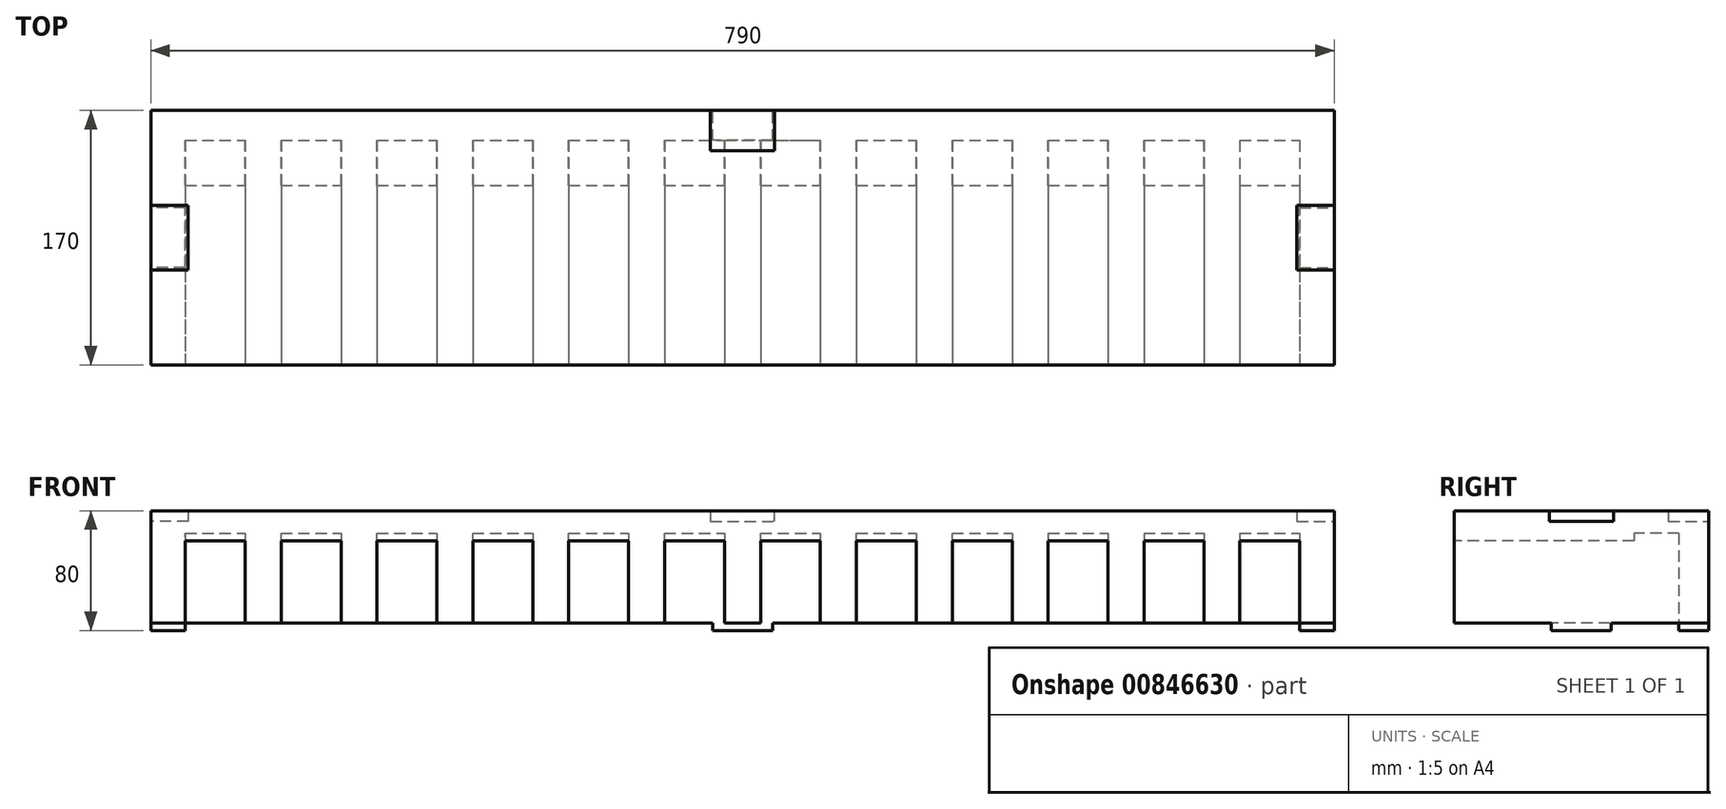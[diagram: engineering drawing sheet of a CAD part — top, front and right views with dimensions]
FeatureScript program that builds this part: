
annotation { "Feature Type Name" : "Feature", "Feature Type Description" : "" }
export const myFeature = defineFeature(function(context is Context, id is Id, definition is map)
    precondition{}
    {
        {
            var Q0;
            Q0=qCreatedBy(makeId("Front.planeOp"),FACE);
            var sketch = newSketch(context, id + "F0", { "sketchPlane" : qUnion([Q0])});
            skLineSegment(sketch, "E0.bottom", {"start": v(-404.78, 0) * mm, "end": v(385.22, 0) * mm});
            skLineSegment(sketch, "E0.top", {"start": v(-404.78, -75) * mm, "end": v(385.22, -75) * mm});
            skLineSegment(sketch, "E0.left", {"start": v(-404.78, 0) * mm, "end": v(-404.78, -75) * mm});
            skLineSegment(sketch, "E0.right", {"start": v(385.22, 0) * mm, "end": v(385.22, -75) * mm});
            skSolve(sketch);
        }
        {
            var Q0;
            Q0=makeQuery(id+"F0.imprint","IMPRINT",FACE,{"disambiguationData":[TD([[makeQuery(id+"F0.imprint","IMPRINT",EDGE,{"derivedFrom":sQuery(id+"F0.wireOp",EDGE,"E0.bottom")}),-1.0]])]});
            extrude(context, id + "F1", {"entities" : qUnion([Q0]), "offsetDistance" : 25 * mm, "depth" : 170 * mm});
        }
        {
            var Q0;
            Q0=makeQuery(id+"F1.opExtrude","CAP_FACE",FACE,{"disambiguationData":[OSD([sQuery(id+"F0.wireOp",EDGE,"E0.bottom"),sQuery(id+"F0.wireOp",EDGE,"E0.top"),sQuery(id+"F0.wireOp",EDGE,"E0.left"),sQuery(id+"F0.wireOp",EDGE,"E0.right")])],"isStart":false});
            var sketch = newSketch(context, id + "F2", { "sketchPlane" : qUnion([Q0])});
            skLineSegment(sketch, "E1.bottom", {"start": v(-381.78, -75) * mm, "end": v(-341.78, -75) * mm});
            skLineSegment(sketch, "E1.top", {"start": v(-381.78, -20) * mm, "end": v(-341.78, -20) * mm});
            skLineSegment(sketch, "E1.left", {"start": v(-381.78, -75) * mm, "end": v(-381.78, -20) * mm});
            skLineSegment(sketch, "E1.right", {"start": v(-341.78, -75) * mm, "end": v(-341.78, -20) * mm});
            skLineSegment(sketch, "E2.bottom", {"start": v(-317.78, -75) * mm, "end": v(-277.78, -75) * mm});
            skLineSegment(sketch, "E2.top", {"start": v(-317.78, -20) * mm, "end": v(-277.78, -20) * mm});
            skLineSegment(sketch, "E2.left", {"start": v(-317.78, -75) * mm, "end": v(-317.78, -20) * mm});
            skLineSegment(sketch, "E2.right", {"start": v(-277.78, -75) * mm, "end": v(-277.78, -20) * mm});
            skLineSegment(sketch, "E3.bottom", {"start": v(-253.78, -75) * mm, "end": v(-213.78, -75) * mm});
            skLineSegment(sketch, "E3.top", {"start": v(-253.78, -20) * mm, "end": v(-213.78, -20) * mm});
            skLineSegment(sketch, "E3.left", {"start": v(-253.78, -75) * mm, "end": v(-253.78, -20) * mm});
            skLineSegment(sketch, "E3.right", {"start": v(-213.78, -75) * mm, "end": v(-213.78, -20) * mm});
            skPoint(sketch, "E4.oppositeSnap0", {"position": v(-233.78, -20) * mm});
            skLineSegment(sketch, "E4.bottom", {"start": v(-189.78, -75) * mm, "end": v(-149.78, -75) * mm});
            skLineSegment(sketch, "E4.top", {"start": v(-189.78, -20) * mm, "end": v(-149.78, -20) * mm});
            skLineSegment(sketch, "E4.left", {"start": v(-189.78, -75) * mm, "end": v(-189.78, -20) * mm});
            skLineSegment(sketch, "E4.right", {"start": v(-149.78, -75) * mm, "end": v(-149.78, -20) * mm});
            skLineSegment(sketch, "E5.bottom", {"start": v(-125.78, -75) * mm, "end": v(-85.78, -75) * mm});
            skLineSegment(sketch, "E5.top", {"start": v(-125.78, -20) * mm, "end": v(-85.78, -20) * mm});
            skLineSegment(sketch, "E5.left", {"start": v(-125.78, -75) * mm, "end": v(-125.78, -20) * mm});
            skLineSegment(sketch, "E5.right", {"start": v(-85.78, -75) * mm, "end": v(-85.78, -20) * mm});
            skLineSegment(sketch, "E6.bottom", {"start": v(-61.78, -75) * mm, "end": v(-21.78, -75) * mm});
            skLineSegment(sketch, "E6.top", {"start": v(-61.78, -20) * mm, "end": v(-21.78, -20) * mm});
            skLineSegment(sketch, "E6.left", {"start": v(-61.78, -75) * mm, "end": v(-61.78, -20) * mm});
            skLineSegment(sketch, "E6.right", {"start": v(-21.78, -75) * mm, "end": v(-21.78, -20) * mm});
            skLineSegment(sketch, "E7.bottom", {"start": v(2.22, -75) * mm, "end": v(42.22, -75) * mm});
            skLineSegment(sketch, "E7.top", {"start": v(2.22, -20) * mm, "end": v(42.22, -20) * mm});
            skLineSegment(sketch, "E7.left", {"start": v(2.22, -75) * mm, "end": v(2.22, -20) * mm});
            skLineSegment(sketch, "E7.right", {"start": v(42.22, -75) * mm, "end": v(42.22, -20) * mm});
            skLineSegment(sketch, "E8.bottom", {"start": v(66.22, -75) * mm, "end": v(106.22, -75) * mm});
            skLineSegment(sketch, "E8.top", {"start": v(66.22, -20) * mm, "end": v(106.22, -20) * mm});
            skLineSegment(sketch, "E8.left", {"start": v(66.22, -75) * mm, "end": v(66.22, -20) * mm});
            skLineSegment(sketch, "E8.right", {"start": v(106.22, -75) * mm, "end": v(106.22, -20) * mm});
            skLineSegment(sketch, "E9.bottom", {"start": v(130.22, -75) * mm, "end": v(170.22, -75) * mm});
            skLineSegment(sketch, "E9.top", {"start": v(130.22, -20) * mm, "end": v(170.22, -20) * mm});
            skLineSegment(sketch, "E9.left", {"start": v(130.22, -75) * mm, "end": v(130.22, -20) * mm});
            skLineSegment(sketch, "E9.right", {"start": v(170.22, -75) * mm, "end": v(170.22, -20) * mm});
            skLineSegment(sketch, "E10.bottom", {"start": v(194.22, -20) * mm, "end": v(234.22, -20) * mm});
            skLineSegment(sketch, "E10.top", {"start": v(194.22, -75) * mm, "end": v(234.22, -75) * mm});
            skLineSegment(sketch, "E10.left", {"start": v(194.22, -20) * mm, "end": v(194.22, -75) * mm});
            skLineSegment(sketch, "E10.right", {"start": v(234.22, -20) * mm, "end": v(234.22, -75) * mm});
            skLineSegment(sketch, "E11.bottom", {"start": v(258.22, -20) * mm, "end": v(298.22, -20) * mm});
            skLineSegment(sketch, "E11.top", {"start": v(258.22, -75) * mm, "end": v(298.22, -75) * mm});
            skLineSegment(sketch, "E11.left", {"start": v(258.22, -20) * mm, "end": v(258.22, -75) * mm});
            skLineSegment(sketch, "E11.right", {"start": v(298.22, -20) * mm, "end": v(298.22, -75) * mm});
            skLineSegment(sketch, "E12.bottom", {"start": v(322.22, -20) * mm, "end": v(362.22, -20) * mm});
            skLineSegment(sketch, "E12.top", {"start": v(322.22, -75) * mm, "end": v(362.22, -75) * mm});
            skLineSegment(sketch, "E12.left", {"start": v(322.22, -20) * mm, "end": v(322.22, -75) * mm});
            skLineSegment(sketch, "E12.right", {"start": v(362.22, -20) * mm, "end": v(362.22, -75) * mm});
            skSolve(sketch);
        }
        {
            var Q0;
            Q0=qSketchRegion(id+"F2",true);
            extrude(context, id + "F3", {"entities" : qUnion([Q0]), "operationType" : NewBodyOperationType.REMOVE, "oppositeDirection" : true, "offsetDistance" : 25 * mm, "depth" : 150 * mm});
        }
        {
            var Q0;
            Q0=makeQuery(id+"F1.opExtrude","SWEPT_FACE",FACE,{"disambiguationData":[OSD([sQuery(id+"F0.wireOp",EDGE,"E0.left")])]});
            var sketch = newSketch(context, id + "F4", { "sketchPlane" : qUnion([Q0])});
            skLineSegment(sketch, "E13", {"start": v(85, 0) * mm, "end": v(106.5, 0) * mm});
            skLineSegment(sketch, "E14", {"start": v(106.5, 0) * mm, "end": v(106.5, -7) * mm});
            skLineSegment(sketch, "E15", {"start": v(106.5, -7) * mm, "end": v(63.5, -7) * mm});
            skLineSegment(sketch, "E16", {"start": v(63.5, -7) * mm, "end": v(63.5, 0) * mm});
            skLineSegment(sketch, "E17", {"start": v(63.5, 0) * mm, "end": v(85, 0) * mm});
            skLineSegment(sketch, "E18", {"start": v(105, -75) * mm, "end": v(105, -80) * mm});
            skLineSegment(sketch, "E19", {"start": v(105, -80) * mm, "end": v(65, -80) * mm});
            skLineSegment(sketch, "E20", {"start": v(65, -80) * mm, "end": v(65, -75) * mm});
            skLineSegment(sketch, "E21", {"start": v(65, -75) * mm, "end": v(105, -75) * mm});
            skSolve(sketch);
        }
        {
            var Q0;
            Q0=makeQuery(id+"F4.imprint","IMPRINT",FACE,{"disambiguationData":[TD([[makeQuery(id+"F4.imprint","IMPRINT",EDGE,{"derivedFrom":sQuery(id+"F4.wireOp",EDGE,"E13")}),1.0]])]});
            var Q1;
            Q1=sQuery(id+"F4.wireOp",EDGE,"E16");
            var Q2;
            Q2=sQuery(id+"F4.wireOp",EDGE,"E15");
            var Q3;
            Q3=sQuery(id+"F4.wireOp",EDGE,"E17");
            var Q4;
            Q4=sQuery(id+"F4.wireOp",EDGE,"E13");
            var Q5;
            Q5=sQuery(id+"F4.wireOp",EDGE,"E14");
            extrude(context, id + "F5", {"entities" : qUnion([Q0]), "operationType" : NewBodyOperationType.REMOVE, "surfaceEntities" : qUnion([Q1, Q2, Q3, Q4, Q5]), "oppositeDirection" : true, "depth" : 25 * mm, "offsetDistance" : 25 * mm});
        }
        {
            var Q0;
            Q0=makeQuery(id+"F4.imprint","IMPRINT",FACE,{"disambiguationData":[TD([[makeQuery(id+"F4.imprint","IMPRINT",EDGE,{"derivedFrom":sQuery(id+"F4.wireOp",EDGE,"E18")}),-1.0]])]});
            var Q1;
            Q1=sQuery(id+"F4.wireOp",EDGE,"xgbccaoA-wlaa-1WH6-teic-Xw8wp0V9t22Q");
            var Q2;
            Q2=sQuery(id+"F4.wireOp",EDGE,"E20");
            var Q3;
            Q3=sQuery(id+"F4.wireOp",EDGE,"E19");
            var Q4;
            Q4=sQuery(id+"F4.wireOp",EDGE,"RcdgaTME-gTL4-fPj2-lDTn-aMnh3h9srcoK");
            var Q5;
            Q5=sQuery(id+"F4.wireOp",EDGE,"E18");
            extrude(context, id + "F6", {"entities" : qUnion([Q0]), "operationType" : NewBodyOperationType.ADD, "surfaceEntities" : qUnion([Q1, Q2, Q3, Q4, Q5]), "oppositeDirection" : true, "depth" : 23 * mm, "offsetDistance" : 25 * mm});
        }
        {
            var Q0;
            Q0=makeQuery(id+"F1.opExtrude","SWEPT_FACE",FACE,{"disambiguationData":[OSD([sQuery(id+"F0.wireOp",EDGE,"E0.right")])]});
            var sketch = newSketch(context, id + "F7", { "sketchPlane" : qUnion([Q0])});
            skLineSegment(sketch, "E22.bottom", {"start": v(-105, -75) * mm, "end": v(-65, -75) * mm});
            skLineSegment(sketch, "E22.top", {"start": v(-105, -80) * mm, "end": v(-65, -80) * mm});
            skLineSegment(sketch, "E22.left", {"start": v(-105, -75) * mm, "end": v(-105, -80) * mm});
            skLineSegment(sketch, "E22.right", {"start": v(-65, -75) * mm, "end": v(-65, -80) * mm});
            skSolve(sketch);
        }
        {
            var Q0;
            Q0 = qSketchRegion(id + "F7", true);
            extrude(context, id + "F8", {"entities" : qUnion([Q0]), "operationType" : NewBodyOperationType.ADD, "oppositeDirection" : true, "depth" : 23 * mm, "offsetDistance" : 25 * mm});
        }
        {
            var Q0;
            Q0=makeQuery(id+"F8.boolean.opBoolean","MERGE",FACE,{"derivedFrom":[makeQuery(id+"F1.opExtrude","SWEPT_FACE",FACE,{"disambiguationData":[OSD([sQuery(id+"F0.wireOp",EDGE,"E0.right")])]}),makeQuery(id+"F8.opExtrude","CAP_FACE",FACE,{"disambiguationData":[OSD([sQuery(id+"F7.wireOp",EDGE,"UznCfJuv-EcPL-bBKx-4p6R-uVAr0uQAR3AA.bottom"),sQuery(id+"F7.wireOp",EDGE,"UznCfJuv-EcPL-bBKx-4p6R-uVAr0uQAR3AA.top"),sQuery(id+"F7.wireOp",EDGE,"UznCfJuv-EcPL-bBKx-4p6R-uVAr0uQAR3AA.left"),sQuery(id+"F7.wireOp",EDGE,"UznCfJuv-EcPL-bBKx-4p6R-uVAr0uQAR3AA.right")])],"isStart":true})]});
            var sketch = newSketch(context, id + "F9", { "sketchPlane" : qUnion([Q0])});
            skLineSegment(sketch, "E23", {"start": v(-85, 0) * mm, "end": v(-63.5, 0) * mm});
            skLineSegment(sketch, "E24", {"start": v(-63.5, 0) * mm, "end": v(-63.5, -7) * mm});
            skLineSegment(sketch, "E25", {"start": v(-63.5, -7) * mm, "end": v(-106.5, -7) * mm});
            skLineSegment(sketch, "E26", {"start": v(-106.5, -7) * mm, "end": v(-106.5, 0) * mm});
            skLineSegment(sketch, "E27", {"start": v(-106.5, 0) * mm, "end": v(-85, 0) * mm});
            skSolve(sketch);
        }
        {
            var Q0;
            Q0 = qSketchRegion(id + "F9", true);
            extrude(context, id + "F10", {"entities" : qUnion([Q0]), "operationType" : NewBodyOperationType.REMOVE, "oppositeDirection" : true, "depth" : 25 * mm, "offsetDistance" : 25 * mm});
        }
        {
            var Q0;
            Q0=makeQuery(id+"F1.opExtrude","CAP_FACE",FACE,{"disambiguationData":[OSD([sQuery(id+"F0.wireOp",EDGE,"E0.bottom"),sQuery(id+"F0.wireOp",EDGE,"E0.top"),sQuery(id+"F0.wireOp",EDGE,"E0.left"),sQuery(id+"F0.wireOp",EDGE,"E0.right")])],"isStart":true});
            var sketch = newSketch(context, id + "F11", { "sketchPlane" : qUnion([Q0])});
            skLineSegment(sketch, "E28", {"start": v(9.78, 0) * mm, "end": v(31.28, 0) * mm});
            skLineSegment(sketch, "E29", {"start": v(31.28, 0) * mm, "end": v(31.28, -7) * mm});
            skLineSegment(sketch, "E30", {"start": v(31.28, -7) * mm, "end": v(-11.72, -7) * mm});
            skLineSegment(sketch, "E31", {"start": v(-11.72, -7) * mm, "end": v(-11.72, 0) * mm});
            skLineSegment(sketch, "E32", {"start": v(-11.72, 0) * mm, "end": v(9.78, 0) * mm});
            skSolve(sketch);
        }
        {
            var Q0;
            Q0 = qSketchRegion(id + "F11", true);
            extrude(context, id + "F12", {"entities" : qUnion([Q0]), "operationType" : NewBodyOperationType.REMOVE, "oppositeDirection" : true, "depth" : 27 * mm, "offsetDistance" : 25 * mm});
        }
        {
            var Q0;
            Q0=makeQuery(id+"F1.opExtrude","CAP_FACE",FACE,{"disambiguationData":[OSD([sQuery(id+"F0.wireOp",EDGE,"E0.bottom"),sQuery(id+"F0.wireOp",EDGE,"E0.top"),sQuery(id+"F0.wireOp",EDGE,"E0.left"),sQuery(id+"F0.wireOp",EDGE,"E0.right")])],"isStart":true});
            var sketch = newSketch(context, id + "F13", { "sketchPlane" : qUnion([Q0])});
            skLineSegment(sketch, "E33.bottom", {"start": v(29.78, -75) * mm, "end": v(-10.22, -75) * mm});
            skLineSegment(sketch, "E33.left", {"start": v(29.78, -75) * mm, "end": v(29.78, -69) * mm});
            skLineSegment(sketch, "E34", {"start": v(-10.22, -75) * mm, "end": v(-10.22, -80) * mm});
            skLineSegment(sketch, "E35", {"start": v(-10.22, -80) * mm, "end": v(29.78, -80) * mm});
            skLineSegment(sketch, "E36", {"start": v(29.78, -80) * mm, "end": v(29.78, -75) * mm});
            skSolve(sketch);
        }
        {
            var Q0;
            Q0 = qSketchRegion(id + "F13", true);
            extrude(context, id + "F14", {"entities" : qUnion([Q0]), "operationType" : NewBodyOperationType.ADD, "oppositeDirection" : true, "depth" : 20 * mm, "offsetDistance" : 25 * mm});
        }
        {
            var Q0;
            Q0=makeQuery(id+"F3.boolean.opBoolean","COPY",FACE,{"derivedFrom":makeQuery(id+"F3.opExtrude","SWEPT_FACE",FACE,{"disambiguationData":[OSD([sQuery(id+"F2.wireOp",EDGE,"E12.bottom")])]})});
            var sketch = newSketch(context, id + "F15", { "sketchPlane" : qUnion([Q0])});
            skLineSegment(sketch, "E37.bottom", {"start": v(-381.78, 50) * mm, "end": v(-341.78, 50) * mm});
            skLineSegment(sketch, "E37.top", {"start": v(-381.78, 20) * mm, "end": v(-341.78, 20) * mm});
            skLineSegment(sketch, "E37.left", {"start": v(-381.78, 50) * mm, "end": v(-381.78, 20) * mm});
            skLineSegment(sketch, "E37.right", {"start": v(-341.78, 50) * mm, "end": v(-341.78, 20) * mm});
            skLineSegment(sketch, "E38.bottom", {"start": v(-317.78, 50) * mm, "end": v(-277.78, 50) * mm});
            skLineSegment(sketch, "E38.top", {"start": v(-317.78, 20) * mm, "end": v(-277.78, 20) * mm});
            skLineSegment(sketch, "E38.left", {"start": v(-317.78, 50) * mm, "end": v(-317.78, 20) * mm});
            skLineSegment(sketch, "E38.right", {"start": v(-277.78, 50) * mm, "end": v(-277.78, 20) * mm});
            skLineSegment(sketch, "E39.bottom", {"start": v(-253.78, 50) * mm, "end": v(-213.78, 50) * mm});
            skLineSegment(sketch, "E39.top", {"start": v(-253.78, 20) * mm, "end": v(-213.78, 20) * mm});
            skLineSegment(sketch, "E39.left", {"start": v(-253.78, 50) * mm, "end": v(-253.78, 20) * mm});
            skLineSegment(sketch, "E39.right", {"start": v(-213.78, 50) * mm, "end": v(-213.78, 20) * mm});
            skLineSegment(sketch, "E40.bottom", {"start": v(-189.78, 50) * mm, "end": v(-149.78, 50) * mm});
            skLineSegment(sketch, "E40.top", {"start": v(-189.78, 20) * mm, "end": v(-149.78, 20) * mm});
            skLineSegment(sketch, "E40.left", {"start": v(-189.78, 50) * mm, "end": v(-189.78, 20) * mm});
            skLineSegment(sketch, "E40.right", {"start": v(-149.78, 50) * mm, "end": v(-149.78, 20) * mm});
            skLineSegment(sketch, "E41.bottom", {"start": v(-125.78, 50) * mm, "end": v(-85.78, 50) * mm});
            skLineSegment(sketch, "E41.top", {"start": v(-125.78, 20) * mm, "end": v(-85.78, 20) * mm});
            skLineSegment(sketch, "E41.left", {"start": v(-125.78, 50) * mm, "end": v(-125.78, 20) * mm});
            skLineSegment(sketch, "E41.right", {"start": v(-85.78, 50) * mm, "end": v(-85.78, 20) * mm});
            skLineSegment(sketch, "E42.bottom", {"start": v(-61.78, 50) * mm, "end": v(-21.78, 50) * mm});
            skLineSegment(sketch, "E42.top", {"start": v(-61.78, 20) * mm, "end": v(-21.78, 20) * mm});
            skLineSegment(sketch, "E42.left", {"start": v(-61.78, 50) * mm, "end": v(-61.78, 20) * mm});
            skLineSegment(sketch, "E42.right", {"start": v(-21.78, 50) * mm, "end": v(-21.78, 20) * mm});
            skLineSegment(sketch, "E43.bottom", {"start": v(2.22, 50) * mm, "end": v(42.22, 50) * mm});
            skLineSegment(sketch, "E43.top", {"start": v(2.22, 20) * mm, "end": v(42.22, 20) * mm});
            skLineSegment(sketch, "E43.left", {"start": v(2.22, 50) * mm, "end": v(2.22, 20) * mm});
            skLineSegment(sketch, "E43.right", {"start": v(42.22, 50) * mm, "end": v(42.22, 20) * mm});
            skLineSegment(sketch, "E44.bottom", {"start": v(66.22, 50) * mm, "end": v(106.22, 50) * mm});
            skLineSegment(sketch, "E44.top", {"start": v(66.22, 20) * mm, "end": v(106.22, 20) * mm});
            skLineSegment(sketch, "E44.left", {"start": v(66.22, 50) * mm, "end": v(66.22, 20) * mm});
            skLineSegment(sketch, "E44.right", {"start": v(106.22, 50) * mm, "end": v(106.22, 20) * mm});
            skPoint(sketch, "E45.firstSnap0", {"position": v(86.22, 50) * mm});
            skLineSegment(sketch, "E45.bottom", {"start": v(130.22, 50) * mm, "end": v(170.22, 50) * mm});
            skLineSegment(sketch, "E45.top", {"start": v(130.22, 20) * mm, "end": v(170.22, 20) * mm});
            skLineSegment(sketch, "E45.left", {"start": v(130.22, 50) * mm, "end": v(130.22, 20) * mm});
            skLineSegment(sketch, "E45.right", {"start": v(170.22, 50) * mm, "end": v(170.22, 20) * mm});
            skLineSegment(sketch, "E46.bottom", {"start": v(194.22, 50) * mm, "end": v(234.22, 50) * mm});
            skLineSegment(sketch, "E46.top", {"start": v(194.22, 20) * mm, "end": v(234.22, 20) * mm});
            skLineSegment(sketch, "E46.left", {"start": v(194.22, 50) * mm, "end": v(194.22, 20) * mm});
            skLineSegment(sketch, "E46.right", {"start": v(234.22, 50) * mm, "end": v(234.22, 20) * mm});
            skLineSegment(sketch, "E47.bottom", {"start": v(258.22, 50) * mm, "end": v(298.22, 50) * mm});
            skLineSegment(sketch, "E47.top", {"start": v(258.22, 20) * mm, "end": v(298.22, 20) * mm});
            skLineSegment(sketch, "E47.left", {"start": v(258.22, 50) * mm, "end": v(258.22, 20) * mm});
            skLineSegment(sketch, "E47.right", {"start": v(298.22, 50) * mm, "end": v(298.22, 20) * mm});
            skLineSegment(sketch, "E48.bottom", {"start": v(322.22, 50) * mm, "end": v(362.22, 50) * mm});
            skLineSegment(sketch, "E48.top", {"start": v(322.22, 20) * mm, "end": v(362.22, 20) * mm});
            skLineSegment(sketch, "E48.left", {"start": v(322.22, 50) * mm, "end": v(322.22, 20) * mm});
            skLineSegment(sketch, "E48.right", {"start": v(362.22, 50) * mm, "end": v(362.22, 20) * mm});
            skSolve(sketch);
        }
        {
            var Q0;
            Q0 = qSketchRegion(id + "F15", true);
            extrude(context, id + "F16", {"entities" : qUnion([Q0]), "operationType" : NewBodyOperationType.REMOVE, "oppositeDirection" : true, "depth" : 5 * mm, "offsetDistance" : 25 * mm});
        }
    });
